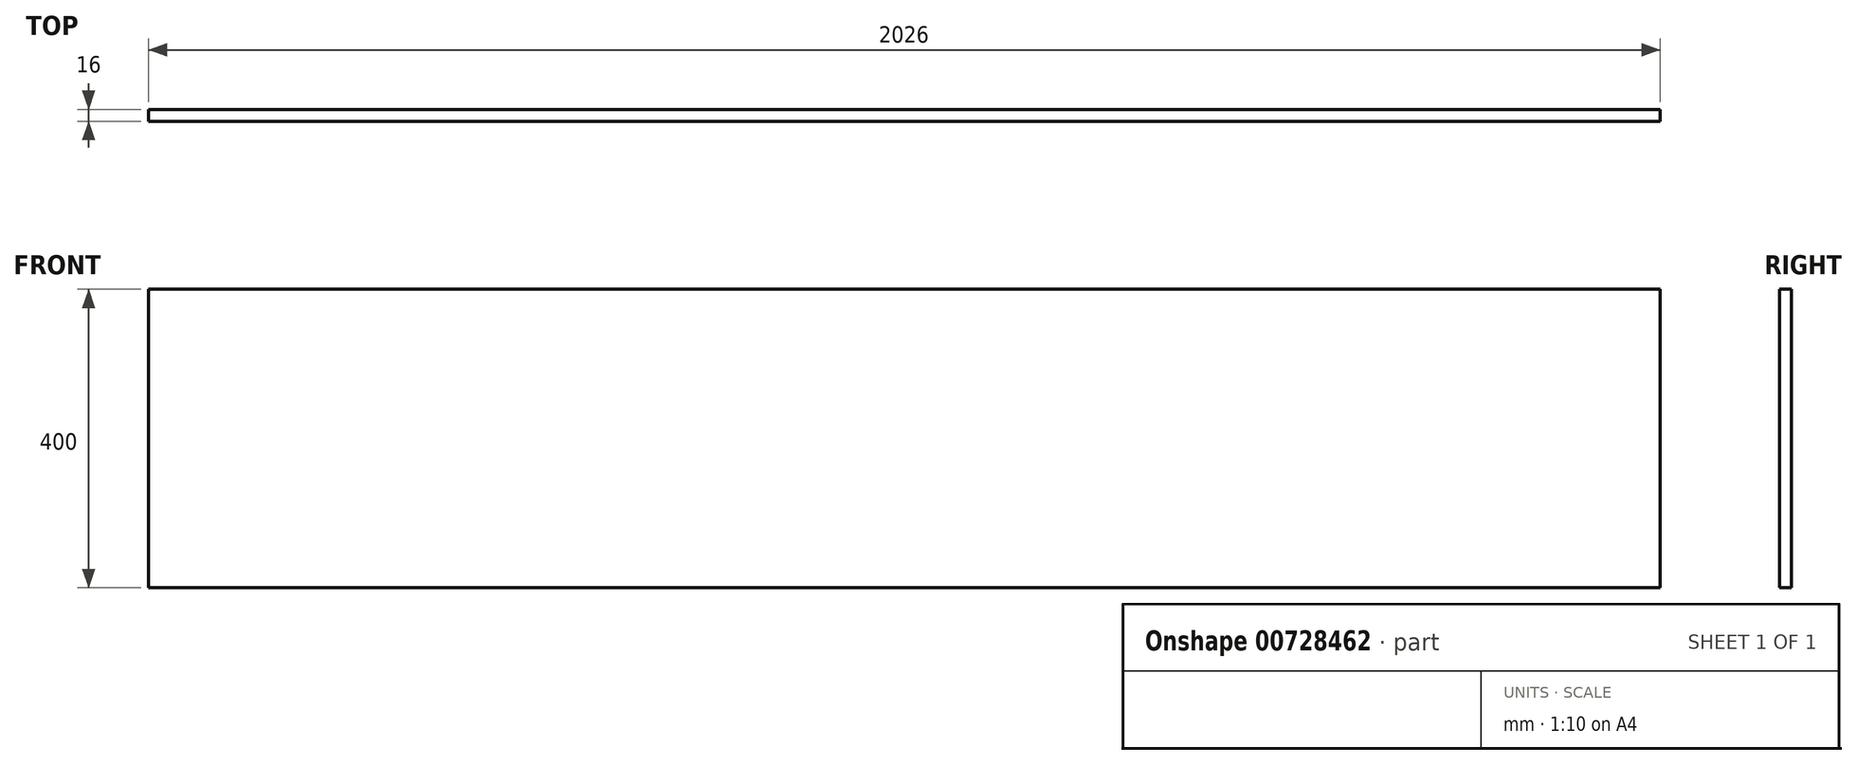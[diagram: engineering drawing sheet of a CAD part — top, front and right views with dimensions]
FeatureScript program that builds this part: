
annotation { "Feature Type Name" : "Feature", "Feature Type Description" : "" }
export const myFeature = defineFeature(function(context is Context, id is Id, definition is map)
    precondition{}
    {
        {
            var Q0;
            Q0=qCreatedBy(makeId("Front.planeOp"),FACE);
            var sketch = newSketch(context, id + "F0", { "sketchPlane" : qUnion([Q0])});
            skLineSegment(sketch, "E0.bottom", {"start": v(0, 0) * mm, "end": v(2026, 0) * mm});
            skLineSegment(sketch, "E0.top", {"start": v(0, 400) * mm, "end": v(2026, 400) * mm});
            skLineSegment(sketch, "E0.left", {"start": v(0, 0) * mm, "end": v(0, 400) * mm});
            skLineSegment(sketch, "E0.right", {"start": v(2026, 0) * mm, "end": v(2026, 400) * mm});
            skSolve(sketch);
        }
        {
            var Q0;
            Q0=makeQuery(id+"F0.imprint","IMPRINT",FACE,{"disambiguationData":[TD([[makeQuery(id+"F0.imprint","IMPRINT",EDGE,{"derivedFrom":sQuery(id+"F0.wireOp",EDGE,"E0.bottom")}),1.0]])]});
            extrude(context, id + "F1", {"entities" : qUnion([Q0]), "depth" : 16 * mm, "offsetDistance" : 25 * mm});
        }
    });
